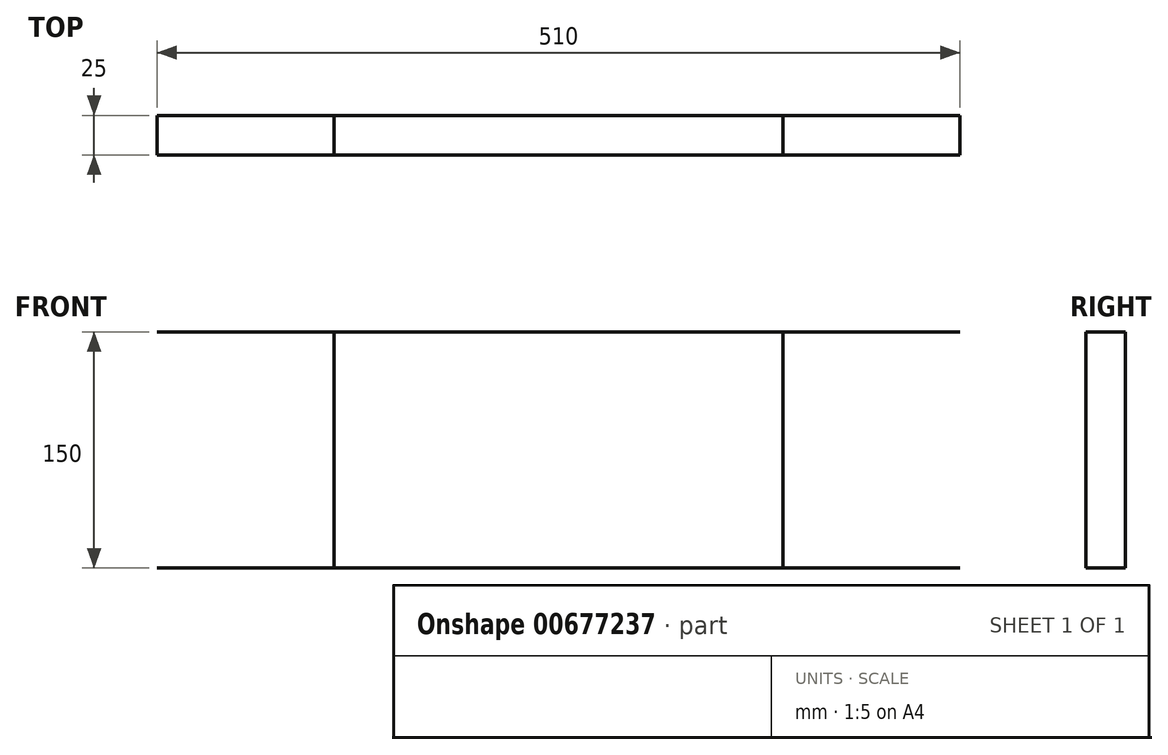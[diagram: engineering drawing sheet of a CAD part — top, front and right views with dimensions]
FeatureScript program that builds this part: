
annotation { "Feature Type Name" : "Feature", "Feature Type Description" : "" }
export const myFeature = defineFeature(function(context is Context, id is Id, definition is map)
    precondition{}
    {
        {
            var Q0;
            Q0=qCreatedBy(makeId("Front.planeOp"),FACE);
            var sketch = newSketch(context, id + "F0", { "sketchPlane" : qUnion([Q0])});
            skLineSegment(sketch, "E0.bottom", {"start": v(-263.5, 127.98) * mm, "end": v(246.5, 127.98) * mm});
            skLineSegment(sketch, "E0.top", {"start": v(-263.5, -172.02) * mm, "end": v(246.5, -172.02) * mm});
            skLineSegment(sketch, "E0.left", {"start": v(-263.5, 127.98) * mm, "end": v(-263.5, -172.02) * mm});
            skLineSegment(sketch, "E0.right", {"start": v(246.5, 127.98) * mm, "end": v(246.5, -172.02) * mm});
            skLineSegment(sketch, "E1", {"start": v(-263.5, 52.98) * mm, "end": v(246.5, 52.98) * mm});
            skLineSegment(sketch, "E2", {"start": v(-263.5, -97.02) * mm, "end": v(246.5, -97.02) * mm});
            skLineSegment(sketch, "E3", {"start": v(-151, 52.98) * mm, "end": v(-151, -97.02) * mm});
            skLineSegment(sketch, "E4", {"start": v(134, 52.98) * mm, "end": v(134, -97.02) * mm});
            skSolve(sketch);
        }
        {
            var Q0;
            Q0=sQuery(id+"F0.wireOp",EDGE,"E3");
            var Q1;
            Q1=sQuery(id+"F0.wireOp",EDGE,"E4");
            extrude(context, id + "F1", {"bodyType" : ToolBodyType.SURFACE, "surfaceEntities" : qUnion([Q0, Q1]), "depth" : 25 * mm, "offsetDistance" : 25 * mm});
        }
        {
            var Q0;
            Q0=sQuery(id+"F0.wireOp",EDGE,"E1");
            var Q1;
            Q1=sQuery(id+"F0.wireOp",EDGE,"E2");
            extrude(context, id + "F2", {"bodyType" : ToolBodyType.SURFACE, "surfaceEntities" : qUnion([Q0, Q1]), "depth" : 25 * mm, "offsetDistance" : 25 * mm});
        }
    });
